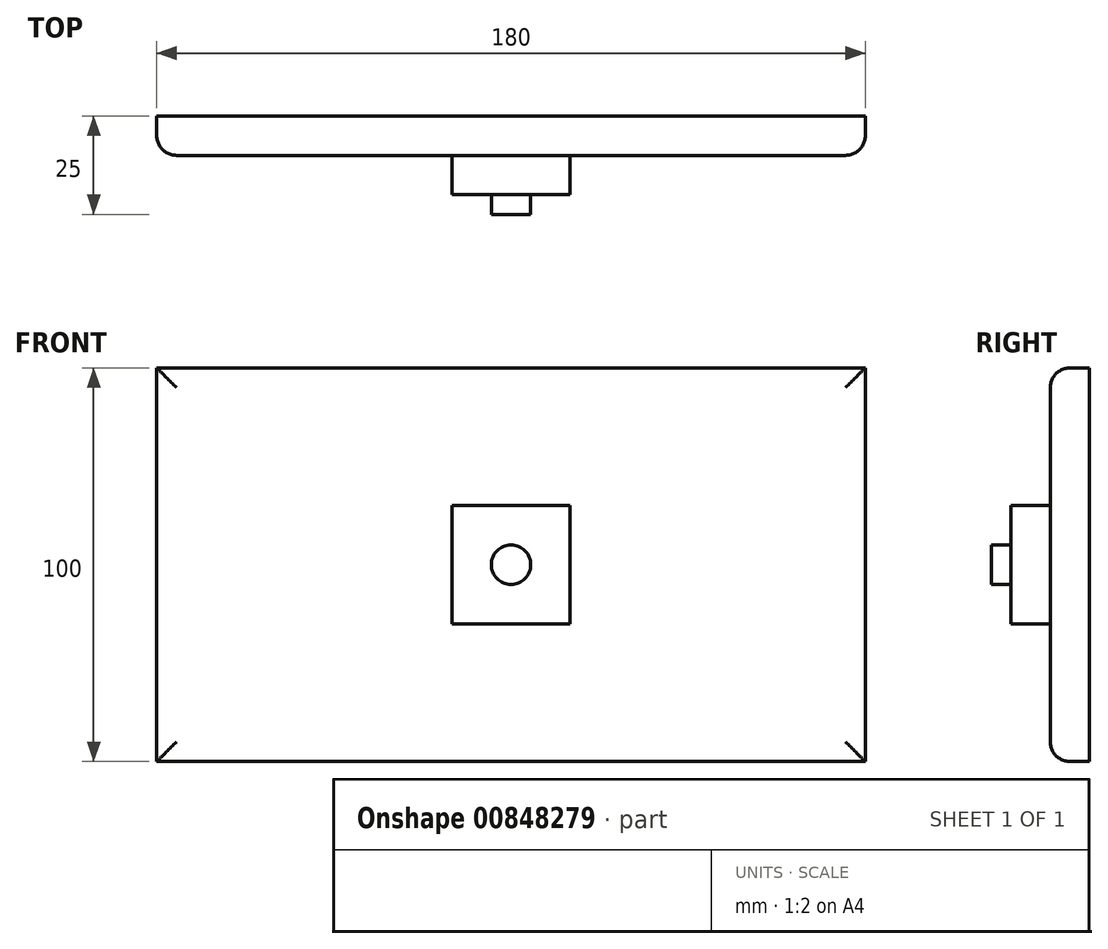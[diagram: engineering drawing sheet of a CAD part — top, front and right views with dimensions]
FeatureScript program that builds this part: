
annotation { "Feature Type Name" : "Feature", "Feature Type Description" : "" }
export const myFeature = defineFeature(function(context is Context, id is Id, definition is map)
    precondition{}
    {
        {
            var Q0;
            Q0=qCreatedBy(makeId("Front.planeOp"),FACE);
            var sketch = newSketch(context, id + "F0", { "sketchPlane" : qUnion([Q0])});
            skLineSegment(sketch, "E0.bottom", {"start": v(-90, 50) * mm, "end": v(90, 50) * mm});
            skLineSegment(sketch, "E0.top", {"start": v(-90, -50) * mm, "end": v(90, -50) * mm});
            skLineSegment(sketch, "E0.left", {"start": v(-90, 50) * mm, "end": v(-90, -50) * mm});
            skLineSegment(sketch, "E0.right", {"start": v(90, 50) * mm, "end": v(90, -50) * mm});
            skSolve(sketch);
        }
        {
            var Q0;
            Q0=makeQuery(id+"F0.imprint","IMPRINT",FACE,{"disambiguationData":[TD([[makeQuery(id+"F0.imprint","IMPRINT",EDGE,{"derivedFrom":sQuery(id+"F0.wireOp",EDGE,"E0.bottom")}),-1.0]])]});
            extrude(context, id + "F1", {"entities" : qUnion([Q0]), "depth" : 10 * mm, "offsetDistance" : 25 * mm});
        }
        {
            var Q0;
            Q0=makeQuery(id+"F1.opExtrude","CAP_FACE",FACE,{"disambiguationData":[OSD([sQuery(id+"F0.wireOp",EDGE,"E0.bottom"),sQuery(id+"F0.wireOp",EDGE,"E0.top"),sQuery(id+"F0.wireOp",EDGE,"E0.left"),sQuery(id+"F0.wireOp",EDGE,"E0.right")])],"isStart":false});
            fillet(context, id + "F2", {"entities" : qUnion([Q0]), "radius" : 5 * mm, "tangentPropagation" : true, "allowEdgeOverflow" : false});
        }
        {
            var Q0;
            Q0=makeQuery(id+"F1.opExtrude","CAP_FACE",FACE,{"disambiguationData":[OSD([sQuery(id+"F0.wireOp",EDGE,"E0.bottom"),sQuery(id+"F0.wireOp",EDGE,"E0.top"),sQuery(id+"F0.wireOp",EDGE,"E0.left"),sQuery(id+"F0.wireOp",EDGE,"E0.right")])],"isStart":false});
            var sketch = newSketch(context, id + "F3", { "sketchPlane" : qUnion([Q0])});
            skLineSegment(sketch, "E1.bottom", {"start": v(-15, 15) * mm, "end": v(15, 15) * mm});
            skLineSegment(sketch, "E1.top", {"start": v(-15, -15) * mm, "end": v(15, -15) * mm});
            skLineSegment(sketch, "E1.left", {"start": v(-15, 15) * mm, "end": v(-15, -15) * mm});
            skLineSegment(sketch, "E1.right", {"start": v(15, 15) * mm, "end": v(15, -15) * mm});
            skSolve(sketch);
        }
        {
            var Q0;
            Q0=makeQuery(id+"F3.imprint","IMPRINT",FACE,{"disambiguationData":[TD([[makeQuery(id+"F3.imprint","IMPRINT",EDGE,{"derivedFrom":sQuery(id+"F3.wireOp",EDGE,"E1.bottom")}),-1.0]])]});
            extrude(context, id + "F4", {"entities" : qUnion([Q0]), "operationType" : NewBodyOperationType.ADD, "depth" : 10 * mm, "offsetDistance" : 25 * mm});
        }
        {
            var Q0;
            Q0=makeQuery(id+"F4.opExtrude","CAP_FACE",FACE,{"disambiguationData":[OSD([sQuery(id+"F3.wireOp",EDGE,"E1.bottom"),sQuery(id+"F3.wireOp",EDGE,"E1.top"),sQuery(id+"F3.wireOp",EDGE,"E1.left"),sQuery(id+"F3.wireOp",EDGE,"E1.right")])],"isStart":false});
            var sketch = newSketch(context, id + "F5", { "sketchPlane" : qUnion([Q0])});
            skCircle(sketch, "E2", {"center": v(0, 0) * mm, "radius": 5 * mm});
            skSolve(sketch);
        }
        {
            var Q0;
            Q0 = qSketchRegion(id + "F5", true);
            extrude(context, id + "F6", {"entities" : qUnion([Q0]), "operationType" : NewBodyOperationType.ADD, "depth" : 5 * mm, "offsetDistance" : 25 * mm});
        }
    });
